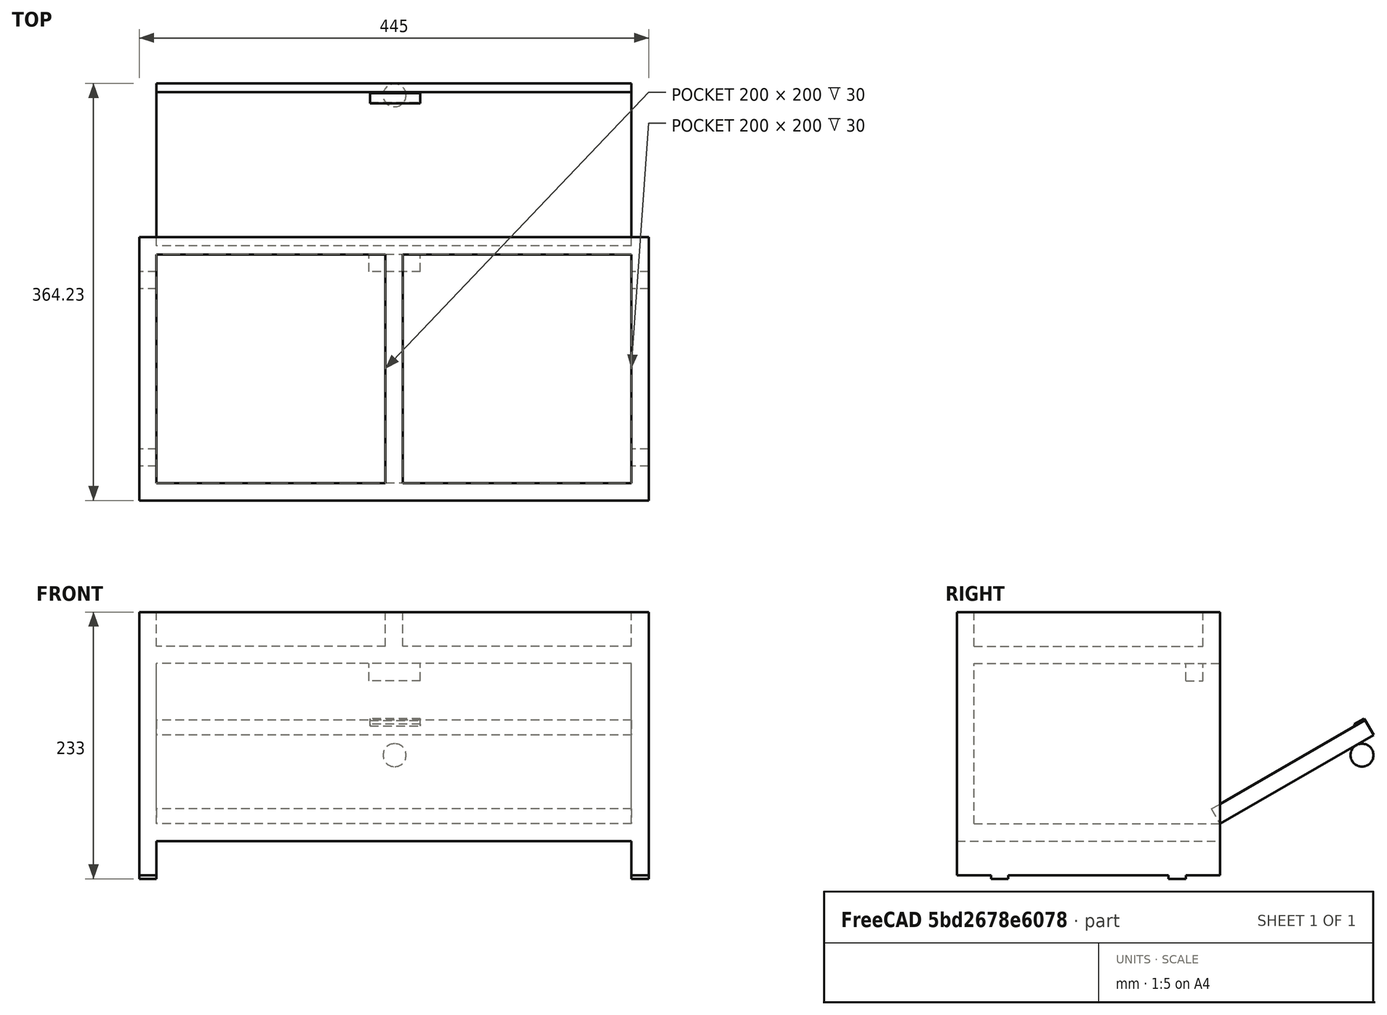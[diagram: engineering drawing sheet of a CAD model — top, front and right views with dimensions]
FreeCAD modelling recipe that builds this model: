
FCSTD DOCUMENT  (FreeCAD 0.17R13522 (Git))
Label: SuporteParaComedouroFusao
License: All rights reserved
LicenseURL: http://en.wikipedia.org/wiki/All_rights_reserved
objects: Part::Box×14, TechDraw::DrawViewDimension×14, TechDraw::DrawViewPart×4, Part::Sphere×1, Part::MultiFuse×1, TechDraw::DrawSVGTemplate×1, TechDraw::DrawPage×1
note: 16 computed .brp shape members not serialized (recipe doc carries the construction recipe); baked Part::Feature solids carry a one-line shape summary decoded from their .brp

FEATURE [Part::Box] Box  label="SuporteLateralVerticalEsquerdo"
  AttacherType = Attacher::AttachEngine3D
  Height = 230
  Length = 230
  Width = 15
FEATURE [Part::Box] Box001  label="TampoSuperiorHorizontal"
  AttacherType = Attacher::AttachEngine3D
  Height = 15
  Length = 215
  Placement = pos=(15,15,185) rot=(0,0,1;0rad)
  Width = 415
FEATURE [Part::Box] Box002  label="SuporteLateralVerticalDireito"
  AttacherType = Attacher::AttachEngine3D
  Height = 230
  Length = 230
  Placement = pos=(0,430,0) rot=(0,0,1;0rad)
  Width = 15
FEATURE [Part::Box] Box003  label="SuporteVerticalMeio"
  AttacherType = Attacher::AttachEngine3D
  Height = 30
  Length = 200
  Placement = pos=(15,215,200) rot=(0,0,1;0rad)
  Width = 15
FEATURE [Part::Box] Box005  label="SuporteFrenteSuperiorVertical"
  AttacherType = Attacher::AttachEngine3D
  Height = 30
  Length = 15
  Placement = pos=(215,15,200) rot=(0,0,1;0rad)
  Width = 415
FEATURE [Part::Box] Box006  label="SuporteFundoInferiorVertical"
  AttacherType = Attacher::AttachEngine3D
  Height = 185
  Length = 15
  Placement = pos=(0,15,45) rot=(0,0,1;0rad)
  Width = 415
FEATURE [Part::Box] Box007  label="TampoInferiorHorizontal"
  AttacherType = Attacher::AttachEngine3D
  Height = 15
  Length = 230
  Placement = pos=(0,15,30) rot=(0,0,1;0rad)
  Width = 415
FEATURE [Part::Box] Box008  label="TampaBasculante"
  AttacherType = Attacher::AttachEngine3D
  Height = 155
  Length = 15
  Placement = pos=(222.5,15,58) rot=(0,1,0;1.0472rad)
  Width = 415
FEATURE [Part::Box] Box010  label="ImaDaMesa SuperiorHorizontal"
  AttacherType = Attacher::AttachEngine3D
  Height = 15
  Length = 15
  Placement = pos=(200,199.5,170) rot=(0,0,1;0rad)
  Width = 45
FEATURE [Part::Box] Box011  label="ChapaDoIma"
  AttacherType = Attacher::AttachEngine3D
  Height = 10
  Length = 2
  Placement = pos=(347,199.5,132) rot=(0,1,0;1.0472rad)
  Width = 44
FEATURE [Part::Sphere] Sphere  label="Puxador"
  Angle1 = -90
  Angle2 = 90
  Angle3 = 360
  AttacherType = Attacher::AttachEngine3D
  Placement = pos=(354,222,105) rot=(0,0,1;0rad)
  Radius = 10
FEATURE [Part::Box] Box012  label="Cube"
  AttacherType = Attacher::AttachEngine3D
  Height = 3
  Length = 15
  Placement = pos=(30,0,-3) rot=(0,0,1;0rad)
  Width = 15
FEATURE [Part::Box] Box013  label="Cube001"
  AttacherType = Attacher::AttachEngine3D
  Height = 3
  Length = 15
  Placement = pos=(185,0,-3) rot=(0,0,1;0rad)
  Width = 15
FEATURE [Part::Box] Box014  label="Cube002"
  AttacherType = Attacher::AttachEngine3D
  Height = 3
  Length = 15
  Placement = pos=(30,430,-3) rot=(0,0,1;0rad)
  Width = 15
FEATURE [Part::Box] Box015  label="Cube003"
  AttacherType = Attacher::AttachEngine3D
  Height = 3
  Length = 15
  Placement = pos=(185,430,-3) rot=(0,0,1;0rad)
  Width = 15
FEATURE [Part::MultiFuse] Fusion
  Placement = pos=(0,0,0) rot=(0,0,1;1.5708rad)
  Shapes = -> [Box,Box001,Box002,Box003,Box005,Box006,Box007,Box008,Box010,Box011,Sphere,Box012,Box013,Box014,Box015]
FEATURE [TechDraw::DrawSVGTemplate] Template
  EditableTexts = AUTHOR_NAME=Sérgio C. G. Alves; DN=DN; DRAWING_TITLE=Tamanho 1; FC-DATE=25/05/2018; FC-REV=REV A; FC-SC=SCALE; FC-SH=X / Y; FC-SI=A3; PN=PN; SI-1=Material: pinho
  Height = 297
  Orientation = 1
  Width = 420
FEATURE [TechDraw::DrawViewPart] View  label="Superior"
  CoarseView = false
  Direction = (0,0,1)
  Focus = 100
  HardHidden = false
  IsoCount = 0
  IsoHidden = false
  IsoVisible = false
  LockPosition = false
  Perspective = false
  Rotation = 90
  Scale = 0.2
  ScaleType = 0
  SeamHidden = false
  SeamVisible = false
  SmoothHidden = false
  SmoothVisible = false
  Source = -> [Fusion]
  X = 339.455
  Y = 209.148
FEATURE [TechDraw::DrawViewPart] View001  label="Lateral"
  CoarseView = false
  Direction = (1,0,0)
  Focus = 100
  HardHidden = false
  IsoCount = 0
  IsoHidden = false
  IsoVisible = false
  LockPosition = false
  Perspective = false
  Rotation = 0
  Scale = 0.25
  ScaleType = 2
  SeamHidden = false
  SeamVisible = false
  SmoothHidden = false
  SmoothVisible = false
  Source = -> [Fusion]
  X = 127.249
  Y = 60.5515
FEATURE [TechDraw::DrawViewPart] View002  label="Frente"
  CoarseView = false
  Direction = (0,1,0)
  Focus = 100
  HardHidden = false
  IsoCount = 0
  IsoHidden = false
  IsoVisible = false
  LockPosition = false
  Perspective = false
  Rotation = 0
  Scale = 0.2
  ScaleType = 0
  SeamHidden = false
  SeamVisible = false
  SmoothHidden = false
  SmoothVisible = false
  Source = -> [Fusion]
  X = 210.149
  Y = 143.378
FEATURE [TechDraw::DrawViewPart] View003  label="Perspectiva"
  CoarseView = false
  Direction = (1,1,1)
  Focus = 100
  HardHidden = false
  IsoCount = 0
  IsoHidden = false
  IsoVisible = false
  LockPosition = false
  Perspective = false
  Rotation = 0
  Scale = 0.2
  ScaleType = 0
  SeamHidden = false
  SeamVisible = false
  SmoothHidden = false
  SmoothVisible = false
  Source = -> [Fusion]
  X = 85.0732
  Y = 225.01
FEATURE [TechDraw::DrawViewDimension] Dimension
  FormatSpec = %.2f
  LockPosition = false
  MeasureType = 1
  References2D = -> [View001]
  Rotation = 0
  Scale = 0.2
  ScaleType = 0
  Type = 2
  X = -54.299
  Y = 2.00181
FEATURE [TechDraw::DrawViewDimension] Dimension001
  FormatSpec = %.2f
  LockPosition = false
  MeasureType = 1
  References2D = -> [View001]
  Rotation = 0
  Scale = 0.2
  ScaleType = 0
  Type = 1
  X = -15.0135
  Y = 38.5348
FEATURE [TechDraw::DrawViewDimension] Dimension003
  FormatSpec = %.2f
  LockPosition = false
  MeasureType = 1
  References2D = -> [View002]
  Rotation = 0
  Scale = 0.2
  ScaleType = 0
  Type = 1
  X = -0.521303
  Y = 32.4946
FEATURE [TechDraw::DrawViewDimension] Dimension004
  FormatSpec = %.2f
  LockPosition = false
  MeasureType = 1
  References2D = -> [View002]
  Rotation = 0
  Scale = 0.2
  ScaleType = 0
  Type = 1
  X = 0.173768
  Y = 39.0978
FEATURE [TechDraw::DrawViewDimension] Dimension005
  FormatSpec = %.2f
  LockPosition = false
  MeasureType = 1
  References2D = -> [View001]
  Rotation = 0
  Scale = 0.2
  ScaleType = 0
  Type = 2
  X = 29.2382
  Y = -29.9235
FEATURE [TechDraw::DrawViewDimension] Dimension006
  FormatSpec = %.2f
  LockPosition = false
  MeasureType = 1
  References2D = -> [View002]
  Rotation = 0
  Scale = 0.2
  ScaleType = 0
  Type = 2
  X = -53.3141
  Y = -26.5733
FEATURE [TechDraw::DrawViewDimension] Dimension008
  FormatSpec = %.2f
  LockPosition = false
  MeasureType = 1
  References2D = -> [View002]
  Rotation = 0
  Scale = 0.2
  ScaleType = 0
  Type = 2
  X = 47.969
  Y = 0.274108
FEATURE [TechDraw::DrawViewDimension] Dimension009
  FormatSpec = %.2f
  LockPosition = false
  MeasureType = 1
  References2D = -> [View002]
  Rotation = 0
  Scale = 0.2
  ScaleType = 0
  Type = 2
  X = -58.6076
  Y = 0.507608
FEATURE [TechDraw::DrawViewDimension] Dimension010
  FormatSpec = %.2f
  LockPosition = false
  MeasureType = 1
  References2D = -> [View002]
  Rotation = 0
  Scale = 0.2
  ScaleType = 0
  Type = 2
  X = -53.1402
  Y = 26.8081
FEATURE [TechDraw::DrawViewDimension] Dimension011
  FormatSpec = %.2f
  LockPosition = false
  MeasureType = 1
  References2D = -> [View]
  Rotation = 0
  Scale = 0.2
  ScaleType = 0
  Type = 2
  X = -59.3902
  Y = -0.456848
FEATURE [TechDraw::DrawViewDimension] Dimension012
  FormatSpec = %.2f
  LockPosition = false
  MeasureType = 1
  References2D = -> [View]
  Rotation = 0
  Scale = 0.2
  ScaleType = 0
  Type = 2
  X = -52.7659
  Y = -0.228424
FEATURE [TechDraw::DrawViewDimension] Dimension013
  FormatSpec = %.2f
  LockPosition = false
  MeasureType = 1
  References2D = -> [View]
  Rotation = 0
  Scale = 0.2
  ScaleType = 0
  Type = 1
  X = -11.878
  Y = 60.5323
FEATURE [TechDraw::DrawViewDimension] Dimension014
  FormatSpec = %.2f
  LockPosition = false
  MeasureType = 1
  References2D = -> [View]
  Rotation = 0
  Scale = 0.2
  ScaleType = 0
  Type = 2
  X = -45.9132
  Y = 20.5581
FEATURE [TechDraw::DrawViewDimension] Dimension015
  FormatSpec = %.2f
  LockPosition = false
  MeasureType = 1
  References2D = -> [View]
  Rotation = 0
  Scale = 0.2
  ScaleType = 0
  Type = 1
  X = -12.1065
  Y = 53.2227
FEATURE [TechDraw::DrawPage] Page
  KeepUpdated = true
  ProjectionType = 0
  Scale = 0.2
  Template = -> Template
  Views = -> [View,View001,View002,View003,Dimension,Dimension001,Dimension003,Dimension004,Dimension005,Dimension006,Dimension008,Dimension009,Dimension010,Dimension011,Dimension012,Dimension013,Dimension014,Dimension015]
